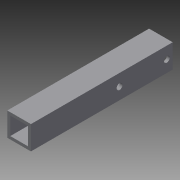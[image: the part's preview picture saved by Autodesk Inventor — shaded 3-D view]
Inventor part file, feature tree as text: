
AUTODESK INVENTOR PART (.ipt)
format: ipt  version: 2015 SP1 (Build 190203100, 203)  size: 101,376 bytes
history: native  units: in
note: dims shown in document units (in); Inventor stores cm internally (conversion verified against a paired STEP export)
features: sketch x3, hole x2, extrude x1
ambient origin geometry x8: Origin, YZ Plane, XZ Plane, XY Plane, X Axis, Y Axis, Z Axis, Center Point
bodies: Solid1 (feature_tree)
feature tree (6):
  extrude  "Extrusion1"  Depth=1.0in
  hole  "Hole1"  [1 undecoded]
  hole  "Hole2"  [1 undecoded]
  sketch  "Sketch1"  dims[d0=1.0in d1=1.0in]
  sketch  "Sketch2"  dims[d2=0.75in d3=0.75in]
  sketch  "Sketch3"  dims[d4=0.125in d5=0.125in d6=6.0in d7=0.0in d8=0.5in d9=0.25in d10=0.5in d11=2.25in d12=0.25in d13=0.75in d14=0.375in d15=0.25in d16=0.5635in d17=0.5in d18=0.8108in d19=2.0in d20=0.5in d21=0.6875in d22=0.75in d23=0.375in d24=0.25in d25=0.5635in d26=1.0in d27=0.8108in]
note: 2 required parameter values undecoded (feature->parameter linkage not recoverable at this tier; creation-order binding heuristic only, values carry confidence <= 0.55)
